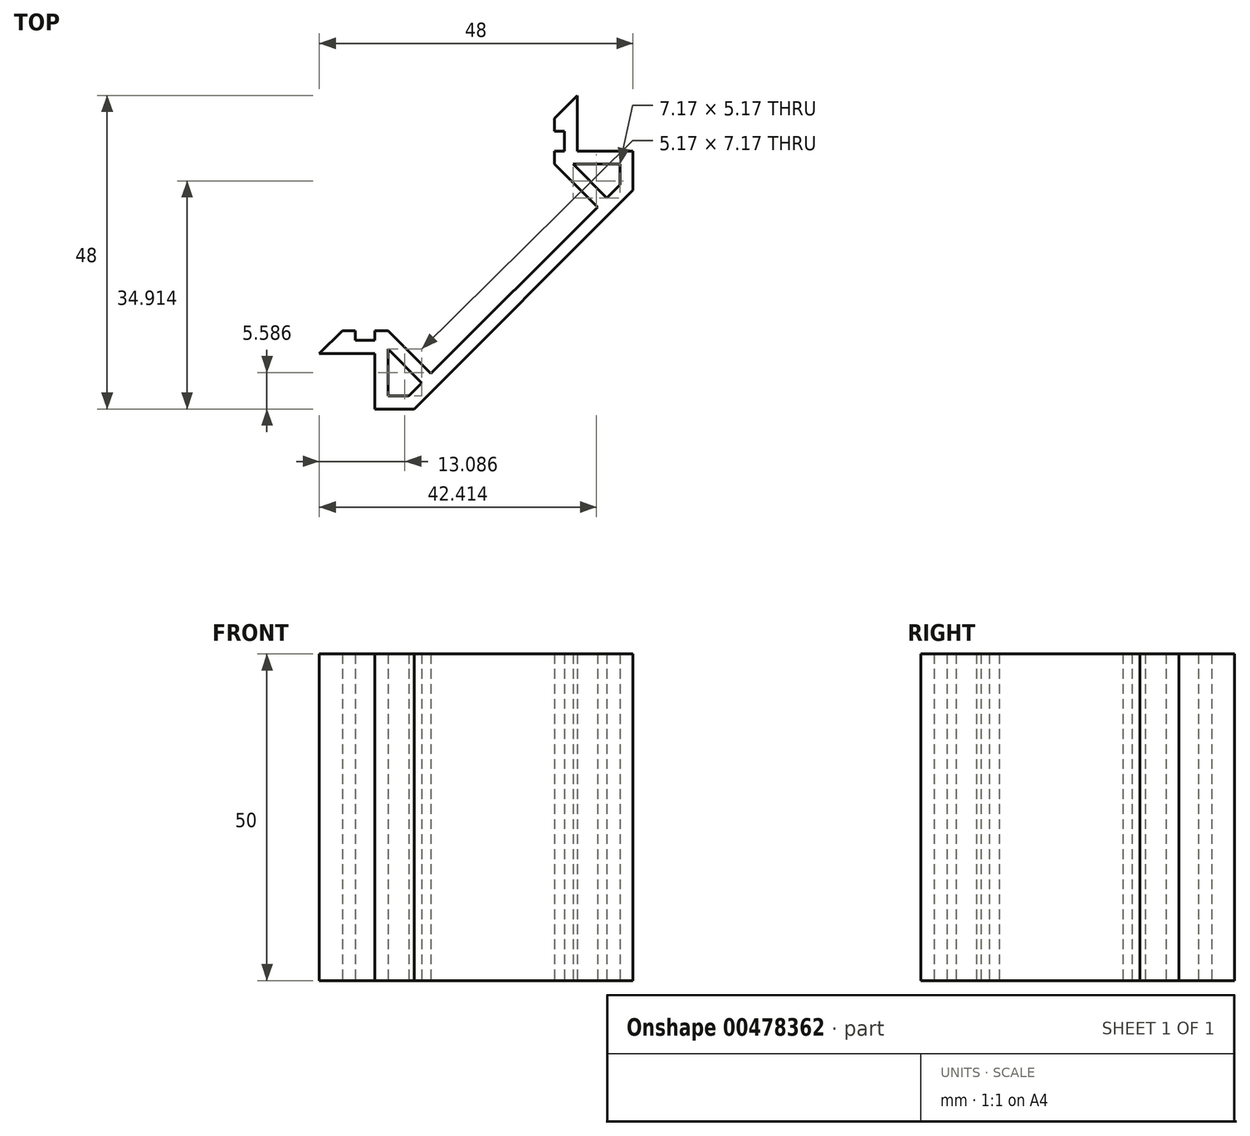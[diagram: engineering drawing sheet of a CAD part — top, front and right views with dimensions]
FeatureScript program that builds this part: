
annotation { "Feature Type Name" : "Feature", "Feature Type Description" : "" }
export const myFeature = defineFeature(function(context is Context, id is Id, definition is map)
    precondition{}
    {
        {
            var Q0;
            Q0=qCreatedBy(makeId("Top.planeOp"),FACE);
            var sketch = newSketch(context, id + "F0", { "sketchPlane" : qUnion([Q0])});
            skLineSegment(sketch, "E0", {"start": v(-68.1, 0) * mm, "end": v(72.16, 0) * mm, "construction": true});
            skLineSegment(sketch, "E1", {"start": v(0, 70.28) * mm, "end": v(0, -61.88) * mm, "construction": true});
            skLineSegment(sketch, "E2.bottom", {"start": v(-19.75, 19.75) * mm, "end": v(19.75, 19.75) * mm, "construction": true});
            skLineSegment(sketch, "E2.top", {"start": v(-19.75, -19.75) * mm, "end": v(19.75, -19.75) * mm, "construction": true});
            skLineSegment(sketch, "E2.left", {"start": v(-19.75, 19.75) * mm, "end": v(-19.75, -19.75) * mm, "construction": true});
            skLineSegment(sketch, "E2.right", {"start": v(19.75, 19.75) * mm, "end": v(19.75, -19.75) * mm, "construction": true});
            skLineSegment(sketch, "E3", {"start": v(-19.75, -19.75) * mm, "end": v(-13.75, -19.75) * mm});
            skLineSegment(sketch, "E4", {"start": v(19.75, 19.75) * mm, "end": v(19.75, 13.75) * mm});
            skLineSegment(sketch, "E5", {"start": v(-13.75, -19.75) * mm, "end": v(19.75, 13.75) * mm});
            skLineSegment(sketch, "E6.0", {"start": v(-19.75, -17.75) * mm, "end": v(-14.58, -17.75) * mm});
            skLineSegment(sketch, "E6.1", {"start": v(-14.58, -17.75) * mm, "end": v(17.75, 14.58) * mm});
            skLineSegment(sketch, "E6.2", {"start": v(17.75, 19.75) * mm, "end": v(17.75, 14.58) * mm});
            skLineSegment(sketch, "E7", {"start": v(-19.75, -19.75) * mm, "end": v(-19.75, -17.75) * mm});
            skLineSegment(sketch, "E8", {"start": v(19.75, 19.75) * mm, "end": v(17.75, 19.75) * mm});
            skSolve(sketch);
        }
        {
            var Q0;
            Q0=qSketchRegion(id+"F0",true);
            extrude(context, id + "F1", {"entities" : qUnion([Q0]), "depth" : 20 * mm});
        }
        {
            var Q0;
            Q0=makeQuery(id+"F1.opExtrude","CAP_FACE",FACE,{"disambiguationData":[OSD([sQuery(id+"F0.wireOp",EDGE,"E3"),sQuery(id+"F0.wireOp",EDGE,"E4"),sQuery(id+"F0.wireOp",EDGE,"E5"),sQuery(id+"F0.wireOp",EDGE,"E6.0"),sQuery(id+"F0.wireOp",EDGE,"E6.1"),sQuery(id+"F0.wireOp",EDGE,"E6.2"),sQuery(id+"F0.wireOp",EDGE,"E7"),sQuery(id+"F0.wireOp",EDGE,"E8")])],"isStart":false});
            var sketch = newSketch(context, id + "F2", { "sketchPlane" : qUnion([Q0])});
            skLineSegment(sketch, "E9.1", {"start": v(-13.75, -19.75) * mm, "end": v(19.75, 13.75) * mm});
            skLineSegment(sketch, "E9.2", {"start": v(19.75, 19.75) * mm, "end": v(19.75, 13.75) * mm});
            skLineSegment(sketch, "E10", {"start": v(19.75, 19.75) * mm, "end": v(11.25, 19.75) * mm});
            skLineSegment(sketch, "E11", {"start": v(17.75, 17.75) * mm, "end": v(17.75, 14.58) * mm});
            skLineSegment(sketch, "E12", {"start": v(17.75, 14.58) * mm, "end": v(15.75, 12.58) * mm});
            skLineSegment(sketch, "E13.left", {"start": v(11.25, 19.75) * mm, "end": v(11.25, 28.25) * mm});
            skLineSegment(sketch, "E14", {"start": v(7.75, 17.75) * mm, "end": v(7.75, 19.75) * mm});
            skLineSegment(sketch, "E15", {"start": v(7.75, 17.75) * mm, "end": v(14.34, 11.16) * mm});
            skLineSegment(sketch, "E16.0", {"start": v(10.58, 17.75) * mm, "end": v(15.75, 12.58) * mm});
            skLineSegment(sketch, "E16.1", {"start": v(17.75, 17.75) * mm, "end": v(10.58, 17.75) * mm});
            skLineSegment(sketch, "E17.trimOffspring", {"start": v(14.34, 11.16) * mm, "end": v(-11.16, -14.34) * mm});
            skLineSegment(sketch, "E18", {"start": v(0, 0) * mm, "end": v(3, -3) * mm, "construction": true});
            skPoint(sketch, "E19.orphan", {"position": v(7.75, 28.25) * mm});
            skLineSegment(sketch, "E20", {"start": v(11.25, 28.25) * mm, "end": v(7.75, 24.75) * mm});
            skLineSegment(sketch, "E21", {"start": v(7.75, 22.75) * mm, "end": v(9.25, 22.75) * mm});
            skLineSegment(sketch, "E22", {"start": v(7.75, 19.75) * mm, "end": v(9.25, 19.75) * mm});
            skLineSegment(sketch, "E23.trimOffspring", {"start": v(9.25, 19.75) * mm, "end": v(9.25, 22.75) * mm});
            skLineSegment(sketch, "E24.trimOffspring", {"start": v(7.75, 22.75) * mm, "end": v(7.75, 24.75) * mm});
            skLineSegment(sketch, "E25.MirrorCS", {"start": v(-19.75, -11.25) * mm, "end": v(-28.25, -11.25) * mm});
            skLineSegment(sketch, "E26.MirrorCS", {"start": v(-17.75, -17.75) * mm, "end": v(-14.58, -17.75) * mm});
            skLineSegment(sketch, "E27.MirrorCS", {"start": v(-22.75, -7.75) * mm, "end": v(-24.75, -7.75) * mm});
            skLineSegment(sketch, "E28.MirrorCS", {"start": v(-17.75, -7.75) * mm, "end": v(-19.75, -7.75) * mm});
            skLineSegment(sketch, "E29.MirrorCS", {"start": v(-17.75, -7.75) * mm, "end": v(-11.16, -14.34) * mm});
            skLineSegment(sketch, "E30.MirrorCS", {"start": v(-17.75, -10.58) * mm, "end": v(-12.58, -15.75) * mm});
            skLineSegment(sketch, "E31.MirrorCS", {"start": v(-19.75, -19.75) * mm, "end": v(-19.75, -11.25) * mm});
            skLineSegment(sketch, "E32.MirrorCS", {"start": v(-22.75, -7.75) * mm, "end": v(-22.75, -9.25) * mm});
            skLineSegment(sketch, "E33.MirrorCS", {"start": v(-19.75, -7.75) * mm, "end": v(-19.75, -9.25) * mm});
            skPoint(sketch, "E34.MirrorP", {"position": v(-28.25, -7.75) * mm});
            skLineSegment(sketch, "E35.MirrorCS", {"start": v(-19.75, -9.25) * mm, "end": v(-22.75, -9.25) * mm});
            skLineSegment(sketch, "E36.MirrorCS", {"start": v(-14.58, -17.75) * mm, "end": v(-12.58, -15.75) * mm});
            skLineSegment(sketch, "E37.MirrorCS", {"start": v(-28.25, -11.25) * mm, "end": v(-24.75, -7.75) * mm});
            skLineSegment(sketch, "E38.MirrorCS", {"start": v(-19.75, -19.75) * mm, "end": v(-13.75, -19.75) * mm});
            skLineSegment(sketch, "E39.MirrorCS", {"start": v(-17.75, -17.75) * mm, "end": v(-17.75, -10.58) * mm});
            skSolve(sketch);
        }
        {
            var Q0;
            Q0=qSketchRegion(id+"F2",true);
            extrude(context, id + "F3", {"entities" : qUnion([Q0]), "operationType" : NewBodyOperationType.ADD, "depth" : 50 * mm});
        }
        {
            var Q0;
            Q0=makeQuery(id+"F3.opExtrude","CAP_FACE",FACE,{"disambiguationData":[OSD([sQuery(id+"F2.wireOp",EDGE,"18LkW5at-QDhS-aThv-tLml-cvOMEycPL9la"),sQuery(id+"F2.wireOp",EDGE,"E9.0"),sQuery(id+"F2.wireOp",EDGE,"E9.1"),sQuery(id+"F2.wireOp",EDGE,"E9.2"),sQuery(id+"F2.wireOp",EDGE,"E10"),sQuery(id+"F2.wireOp",EDGE,"E11"),sQuery(id+"F2.wireOp",EDGE,"E12"),sQuery(id+"F2.wireOp",EDGE,"gG7GE99v-zfpN-SBz3-vrGv-1yJCzINz42Ef"),sQuery(id+"F2.wireOp",EDGE,"UVh0vROw-WSek-6lxM-BEad-8BDBskrnTNki"),sQuery(id+"F2.wireOp",EDGE,"I0wHJKti-MazQ-Kak2-dpeP-lC7VClrsx2uq"),sQuery(id+"F2.wireOp",EDGE,"xpxs7AxX-igCE-9d4T-wt1V-guV83atNUd22"),sQuery(id+"F2.wireOp",EDGE,"PK7llsSc-NEYg-9CMv-nXlP-JqZKifBTAgQ1"),sQuery(id+"F2.wireOp",EDGE,"E13.top"),sQuery(id+"F2.wireOp",EDGE,"E13.left"),sQuery(id+"F2.wireOp",EDGE,"E13.right"),sQuery(id+"F2.wireOp",EDGE,"klJwY84u-2a2g-KLa0-gFfR-2CacjcHoM4EU")])],"isStart":false});
            var sketch = newSketch(context, id + "F4", { "sketchPlane" : qUnion([Q0])});
            skLineSegment(sketch, "E40.0", {"start": v(19.75, 19.75) * mm, "end": v(19.75, 13.75) * mm});
            skLineSegment(sketch, "E40.1.0", {"start": v(19.75, 19.75) * mm, "end": v(19.75, 13.75) * mm});
            skLineSegment(sketch, "E40.1.1", {"start": v(19.75, 13.75) * mm, "end": v(-13.75, -19.75) * mm});
            skLineSegment(sketch, "E40.1.2", {"start": v(-13.75, -19.75) * mm, "end": v(-19.75, -19.75) * mm});
            skLineSegment(sketch, "E40.1.3", {"start": v(-19.75, -19.75) * mm, "end": v(-19.75, -17.75) * mm});
            skLineSegment(sketch, "E40.1.4", {"start": v(-19.75, -17.75) * mm, "end": v(-14.58, -17.75) * mm});
            skLineSegment(sketch, "E40.1.5", {"start": v(-14.58, -17.75) * mm, "end": v(17.75, 14.58) * mm});
            skLineSegment(sketch, "E40.1.6", {"start": v(17.75, 14.58) * mm, "end": v(17.75, 19.75) * mm});
            skLineSegment(sketch, "E40.1.7", {"start": v(17.75, 19.75) * mm, "end": v(19.75, 19.75) * mm});
            skSolve(sketch);
        }
        {
            var Q0;
            Q0=makeQuery(id+"F1.opExtrude","CAP_FACE",FACE,{"disambiguationData":[OSD([sQuery(id+"F0.wireOp",EDGE,"E3"),sQuery(id+"F0.wireOp",EDGE,"E4"),sQuery(id+"F0.wireOp",EDGE,"E5"),sQuery(id+"F0.wireOp",EDGE,"E6.0"),sQuery(id+"F0.wireOp",EDGE,"E6.1"),sQuery(id+"F0.wireOp",EDGE,"E6.2"),sQuery(id+"F0.wireOp",EDGE,"E7"),sQuery(id+"F0.wireOp",EDGE,"E8")])],"isStart":true});
            var Q1;
            {var subQ0=sQuery(id+"F2.wireOp",EDGE,"E15");var subQ1=sQuery(id+"F2.wireOp",EDGE,"NpaF42hW-VqID-WalX-XxEA-2YMa1CjjjRY0");var subQ2=sQuery(id+"F2.wireOp",EDGE,"E13.left");var subQ3=sQuery(id+"F2.wireOp",EDGE,"E11");var subQ4=sQuery(id+"F2.wireOp",EDGE,"E12");var subQ5=sQuery(id+"F2.wireOp",EDGE,"E10");var subQ6=sQuery(id+"F2.wireOp",EDGE,"E14");var subQ7=sQuery(id+"F2.wireOp",EDGE,"7b85fce7-b53d-4be7-b1e5-ed8bc669a566.trimOffspring");var subQ8=sQuery(id+"F2.wireOp",EDGE,"E16.0");var subQ9=sQuery(id+"F2.wireOp",EDGE,"E16.1");var subQ10=sQuery(id+"F2.wireOp",EDGE,"E17.trimOffspring");var subQ11=sQuery(id+"F2.wireOp",EDGE,"bbbeae94-ef78-47c9-bc7a-b52c7598cb07.0");var subQ12=sQuery(id+"F2.wireOp",EDGE,"bf28c3a9-25f4-4f9d-b41c-3f9bea3826a2.0");var subQ13=sQuery(id+"F2.wireOp",EDGE,"MSiZ2p9g-kzmG-F0xN-plco-kywUhb0tRkwM");var subQ14=sQuery(id+"F2.wireOp",EDGE,"2058a7e1-57a1-48df-9df2-63a8aff02368.trimOffspring");Q1=makeQuery(id+"F3.boolean.opBoolean","SPLIT",FACE,{"disambiguationData":[TD([makeQuery(id+"F1.opExtrude","SWEPT_FACE",FACE,{"disambiguationData":[OSD([sQuery(id+"F0.wireOp",EDGE,"E6.2")])]})])],"derivedFrom":makeQuery(id+"F3.opExtrude","CAP_FACE",FACE,{"disambiguationData":[OSD([sQuery(id+"F2.wireOp",EDGE,"E9.1"),sQuery(id+"F2.wireOp",EDGE,"E9.2"),subQ5,subQ3,subQ4,subQ2,subQ6,subQ1,subQ0,subQ8,subQ9,subQ10,subQ11,subQ12,subQ13,subQ14,sQuery(id+"F2.wireOp",EDGE,"1a46eb31-a125-4b13-a039-934298ed064b0.MirrorCS"),sQuery(id+"F2.wireOp",EDGE,"1a46eb31-a125-4b13-a039-934298ed064b1.MirrorCS"),sQuery(id+"F2.wireOp",EDGE,"1a46eb31-a125-4b13-a039-934298ed064b2.MirrorCS"),sQuery(id+"F2.wireOp",EDGE,"1a46eb31-a125-4b13-a039-934298ed064b3.MirrorCS"),sQuery(id+"F2.wireOp",EDGE,"1a46eb31-a125-4b13-a039-934298ed064b4.MirrorCS"),sQuery(id+"F2.wireOp",EDGE,"1a46eb31-a125-4b13-a039-934298ed064b5.MirrorCS"),sQuery(id+"F2.wireOp",EDGE,"1a46eb31-a125-4b13-a039-934298ed064b6.MirrorCS"),sQuery(id+"F2.wireOp",EDGE,"1a46eb31-a125-4b13-a039-934298ed064b7.MirrorCS"),sQuery(id+"F2.wireOp",EDGE,"1a46eb31-a125-4b13-a039-934298ed064b9.MirrorCS"),sQuery(id+"F2.wireOp",EDGE,"1a46eb31-a125-4b13-a039-934298ed064b10.MirrorCS"),sQuery(id+"F2.wireOp",EDGE,"1a46eb31-a125-4b13-a039-934298ed064b11.MirrorCS"),sQuery(id+"F2.wireOp",EDGE,"1a46eb31-a125-4b13-a039-934298ed064b12.MirrorCS"),sQuery(id+"F2.wireOp",EDGE,"1a46eb31-a125-4b13-a039-934298ed064b13.MirrorCS"),subQ7])],"isStart":true})});}
            extrude(context, id + "F5", {"entities" : qUnion([Q0]), "operationType" : NewBodyOperationType.REMOVE, "endBound" : BoundingType.UP_TO_SURFACE, "oppositeDirection" : true, "endBoundEntityFace" : qUnion([Q1]), "depth" : 25 * mm});
        }
    });
